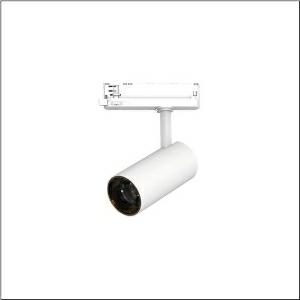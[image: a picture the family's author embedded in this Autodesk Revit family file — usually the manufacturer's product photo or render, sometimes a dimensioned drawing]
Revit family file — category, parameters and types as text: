
# Revit family: spot_31_slim_51sf137fa2b
name_source: partatom
category: Lighting Fixtures
units: mm (PartAtom-declared; Revit-internal decimal feet)

## family parameters
Cut with Voids When Loaded = No
Host = Face
Light Source = No
Part Type = Normal
Room Calculation Point = No
Round Connector Dimension = Use Diameter
Shared = No

## types (1)
- Spot 31 Slim (1 x LED, 2150 lm, 17.6 W, 2700K)
    Apparent Load = 18 VA
    CIE Flux Codes = 97 100 100 100 100
    Color Rendering = 90
    Color Temperature = 2700K
    Default Elevation = 1800 mm
    Description = Spot 31 Slim, directional spotlight, light control with reflector, of aluminium, LED rated luminous flux: 2.150lm, light colour: 927, control gear: ECG, with 3-phase adapter, mains connection: 220..240V, AC, 50/60Hz, housing, of aluminium, traffic white (RAL 9016), diameter: 70mm, adapter, of plastic, protection rating (complete): IP20, insulation class (complete): insulation class I (protective earthing), certification: CE, impact resistance: IK02, packaging unit: 1 piece
    Height = 210 mm
    Lamp = 1 x LED
    Lamp Light Flux = 2150 lm
    Lamp Power = 17.6 W
    Lamp count = 1
    Length = 70 mm
    Luminous efficacy = 122 lm/W
    Manufacturer = Siteco
    ModVariant = No
    Model = 51SF137FA2B
    Mounting Place = Ceiling
    Mounting Type = Pendant
    Number of Poles = 1
    OnlyDefault = Yes
    Power Factor = 1
    Product Name = Spot 31 Slim
    Product group = directional spotlight
    ProductGroupID = 906
    Protection Class = Protection class I
    Protection Degree = IP 20
    RLX_Detail_Level = 1
    RLX_Emergency_Light_Flux = 0 lm
    RLX_Emergency_Type = 0
    RLX_Emergency_Type_DB = No
    RlxData = <blob elided: 14149 chars, md5=c35adca6>
    Socket = socket
    Standby Power = 0 W
    System Light Flux = 2150 lm
    System Power = 18 W
    Type Comments = Product without accessories
    Type Image = l_1228468.jpg
    URL = http://relux.com
    VarID = ---
    Voltage = 0 V
    Weight = 0.00 kg
    Width = 0 mm  [stored 0 ft]

note: [stored X ft] marks values corroborated as IEEE doubles in the binary element streams (Revit-internal decimal feet)

## geometry (parser evidence)
native form markers: Sweep x13
no freeform markers — native parametric forms only
